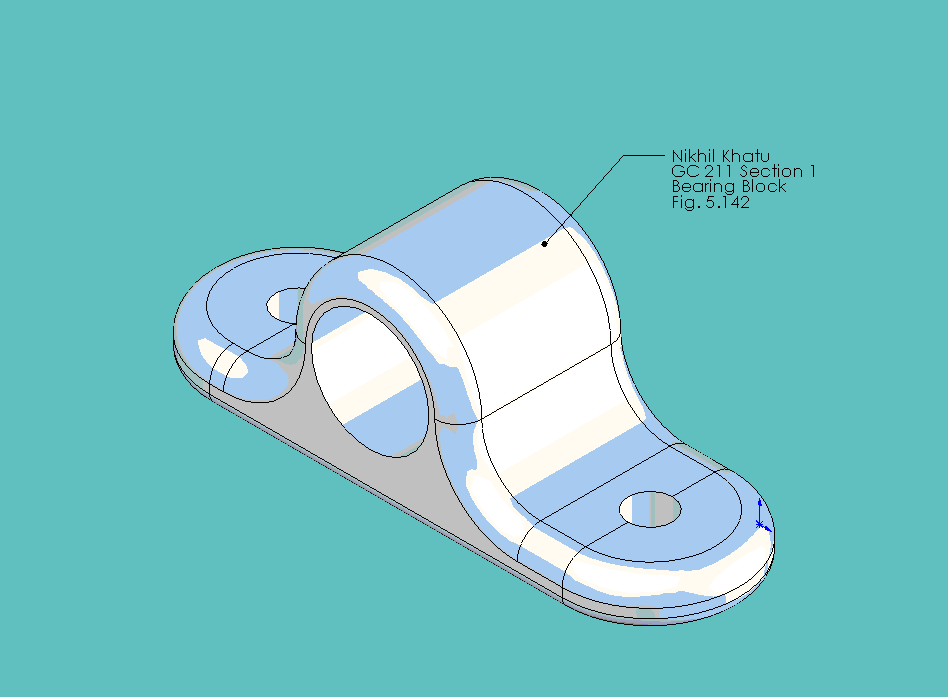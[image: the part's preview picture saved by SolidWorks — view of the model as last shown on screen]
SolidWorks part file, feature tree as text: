
SOLIDWORKS PART (.sldprt)
format: sldprt  version: not decoded by parser v0  size: 593,920 bytes
history: native  units: mm
features: sketch x6, cut_extrude x5, fillet x4, plane x3, material x1, extrude x1 (+11 scaffold rows collapsed)
feature tree (31):
  scaffold x11  (default folders/planes/origin — collapsed)
  material  "E-Glass Fiber"
  plane  "Frontal"
  plane  "Horizontal"
  plane  "Profile"
  sketch  "Sketch1"  dims[D1=38.1mm]
  extrude  "Extrude1"  Depth=20.6248mm
  sketch  "Sketch2"  dims[D1=9.525mm]
  cut_extrude  "Cut-Extrude1"  [1 undecoded]
  sketch  "Sketch3"  dims[D1=4.7752mm]
  cut_extrude  "Cut-Extrude2"  [1 undecoded]
  sketch  "Sketch4"
  cut_extrude  "Cut-Extrude3"  [1 undecoded]
  sketch  "Sketch5"  dims[D1=4.7752mm]
  cut_extrude  "Cut-Extrude4"  Depth=20.6248mm
  sketch  "Sketch7"
  cut_extrude  "Cut-Extrude6"  [1 undecoded]
  fillet  "Fillet1"  Radius=6.35mm
  fillet  "Fillet3"  Radius=6.35mm
  fillet  "Fillet4"  Radius=2.54mm
  fillet  "Fillet6"  Radius=1.27mm
decode coverage: 10 of 16 modeling features carry decoded parameters
note: 4 parameter values undecoded
summary: no parameter record found for 4 features
note: suppression state not decoded; provenance and decode notes live in map.json
